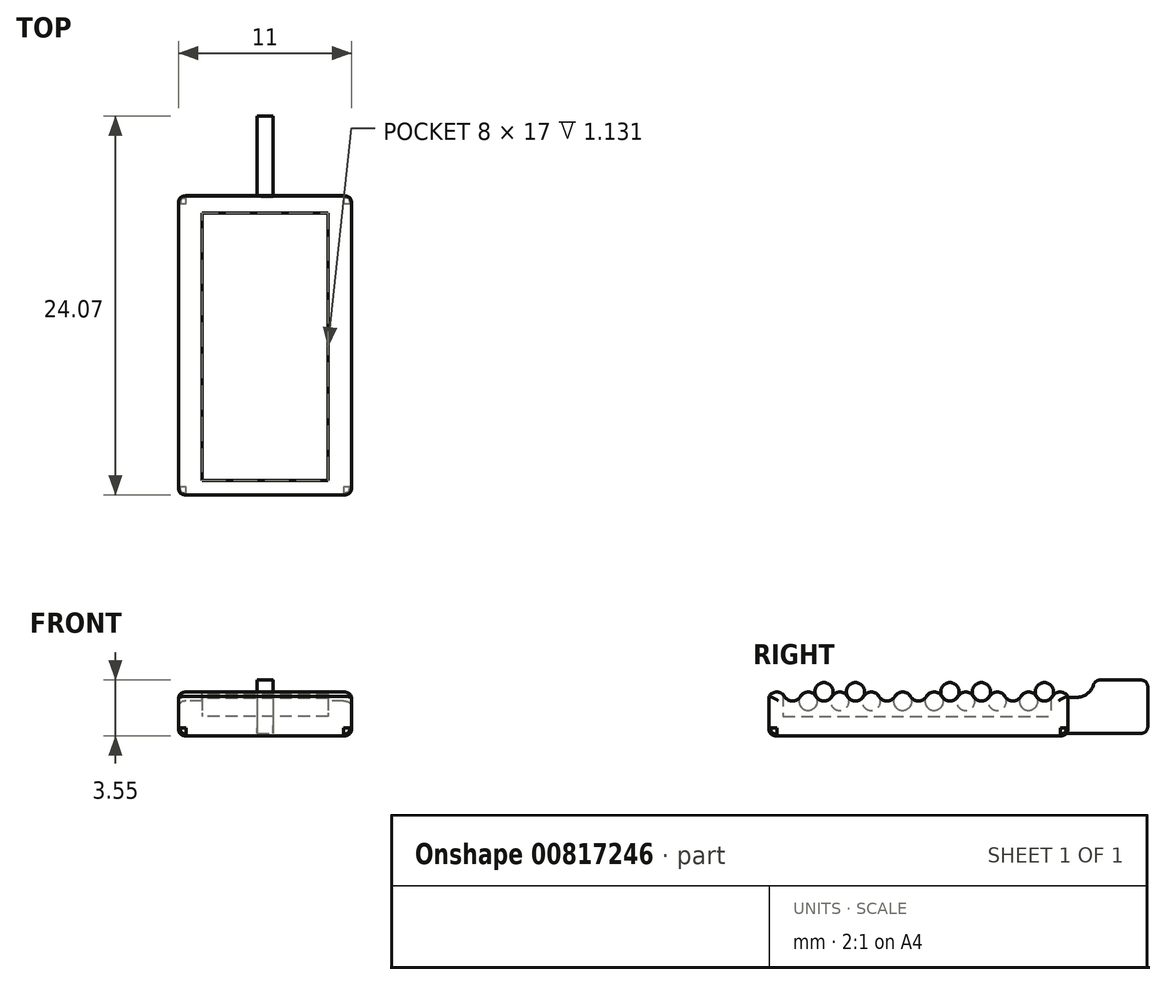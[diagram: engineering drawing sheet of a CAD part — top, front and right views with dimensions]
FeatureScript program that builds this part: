
annotation { "Feature Type Name" : "Feature", "Feature Type Description" : "" }
export const myFeature = defineFeature(function(context is Context, id is Id, definition is map)
    precondition{}
    {
        {
            var Q0;
            Q0=qCreatedBy(makeId("Right.planeOp"),FACE);
            var sketch = newSketch(context, id + "F0", { "sketchPlane" : qUnion([Q0])});
            skLineSegment(sketch, "E0.bottom", {"start": v(9.6, -1.25) * mm, "end": v(-9.4, -1.25) * mm});
            skArc(sketch, "E1.18.0.0", {"start": v(9.59, 1.26) * mm, "mid": v(9.09, 1.53) * mm, "end": v(8.6, 1.25) * mm});
            skLineSegment(sketch, "E2", {"start": v(-9.4, 1.25) * mm, "end": v(-9.4, 1.25) * mm});
            skArc(sketch, "E3.2.0.0", {"start": v(7.6, 1.25) * mm, "mid": v(7.1, 1.53) * mm, "end": v(6.6, 1.25) * mm});
            skArc(sketch, "E3.4.0.0", {"start": v(5.6, 1.25) * mm, "mid": v(5.1, 1.53) * mm, "end": v(4.6, 1.25) * mm});
            skArc(sketch, "E3.6.0.0", {"start": v(3.6, 1.25) * mm, "mid": v(3.1, 1.53) * mm, "end": v(2.6, 1.25) * mm});
            skArc(sketch, "E3.8.0.0", {"start": v(1.6, 1.25) * mm, "mid": v(1.1, 1.53) * mm, "end": v(0.6, 1.25) * mm});
            skArc(sketch, "E3.10.0.0", {"start": v(-0.4, 1.25) * mm, "mid": v(-0.9, 1.53) * mm, "end": v(-1.4, 1.25) * mm});
            skArc(sketch, "E3.12.0.0", {"start": v(-2.4, 1.25) * mm, "mid": v(-2.9, 1.53) * mm, "end": v(-3.4, 1.25) * mm});
            skArc(sketch, "E3.14.0.0", {"start": v(-4.4, 1.25) * mm, "mid": v(-4.9, 1.53) * mm, "end": v(-5.4, 1.25) * mm});
            skArc(sketch, "E3.16.0.0", {"start": v(-6.4, 1.25) * mm, "mid": v(-6.9, 1.53) * mm, "end": v(-7.4, 1.25) * mm});
            skArc(sketch, "E3.18.0.0", {"start": v(-8.4, 1.25) * mm, "mid": v(-8.9, 1.53) * mm, "end": v(-9.4, 1.26) * mm});
            skArc(sketch, "E4.MirrorCS", {"start": v(-1.4, 1.25) * mm, "mid": v(-1.9, 0.97) * mm, "end": v(-2.4, 1.25) * mm});
            skArc(sketch, "E5.MirrorCS", {"start": v(0.6, 1.25) * mm, "mid": v(0.1, 0.97) * mm, "end": v(-0.4, 1.25) * mm});
            skArc(sketch, "E6.MirrorCS", {"start": v(2.6, 1.25) * mm, "mid": v(2.1, 0.97) * mm, "end": v(1.6, 1.25) * mm});
            skArc(sketch, "E7.MirrorCS", {"start": v(4.6, 1.25) * mm, "mid": v(4.1, 0.97) * mm, "end": v(3.6, 1.25) * mm});
            skArc(sketch, "E8.MirrorCS", {"start": v(6.6, 1.25) * mm, "mid": v(6.1, 0.97) * mm, "end": v(5.6, 1.25) * mm});
            skArc(sketch, "E9.MirrorCS", {"start": v(8.6, 1.25) * mm, "mid": v(8.1, 0.97) * mm, "end": v(7.6, 1.25) * mm});
            skArc(sketch, "E10.MirrorCS", {"start": v(-3.4, 1.25) * mm, "mid": v(-3.9, 0.97) * mm, "end": v(-4.4, 1.25) * mm});
            skArc(sketch, "E11.MirrorCS", {"start": v(-5.4, 1.25) * mm, "mid": v(-5.9, 0.97) * mm, "end": v(-6.4, 1.25) * mm});
            skArc(sketch, "E12.MirrorCS", {"start": v(-7.4, 1.25) * mm, "mid": v(-7.9, 0.97) * mm, "end": v(-8.4, 1.25) * mm});
            skLineSegment(sketch, "E13", {"start": v(9.6, 1.24) * mm, "end": v(9.6, -1.25) * mm});
            skLineSegment(sketch, "E14", {"start": v(-9.4, 1.24) * mm, "end": v(-9.4, -1.25) * mm});
            skPoint(sketch, "E15.visualSharp", {"position": v(-9.4, 1.25) * mm});
            skArc(sketch, "E15.filletArc", {"start": v(-9.4, 1.26) * mm, "mid": v(-9.4, 1.25) * mm, "end": v(-9.4, 1.24) * mm});
            skPoint(sketch, "E16.visualSharp", {"position": v(9.6, 1.25) * mm});
            skArc(sketch, "E16.filletArc", {"start": v(9.6, 1.24) * mm, "mid": v(9.6, 1.25) * mm, "end": v(9.59, 1.26) * mm});
            skSolve(sketch);
        }
        {
            var Q0;
            Q0 = qSketchRegion(id + "F0", true);
            extrude(context, id + "F1", {"entities" : qUnion([Q0]), "depth" : 11 * mm, "offsetDistance" : 25 * mm});
        }
        {
            var Q0;
            Q0=qCreatedBy(makeId("Top.planeOp"),FACE);
            var sketch = newSketch(context, id + "F2", { "sketchPlane" : qUnion([Q0])});
            skLineSegment(sketch, "E17", {"start": v(0, 0) * mm, "end": v(11, 0) * mm});
            skLineSegment(sketch, "E18.bottom", {"start": v(9.5, -8.5) * mm, "end": v(1.5, -8.5) * mm});
            skLineSegment(sketch, "E18.top", {"start": v(9.5, 8.5) * mm, "end": v(1.5, 8.5) * mm});
            skLineSegment(sketch, "E18.left", {"start": v(9.5, -8.5) * mm, "end": v(9.5, 8.5) * mm});
            skLineSegment(sketch, "E18.right", {"start": v(1.5, -8.5) * mm, "end": v(1.5, 8.5) * mm});
            skPoint(sketch, "E18.middle", {"position": v(5.5, 0) * mm});
            skSolve(sketch);
        }
        {
            var Q0;
            Q0 = qSketchRegion(id + "F2", true);
            extrude(context, id + "F3", {"entities" : qUnion([Q0]), "operationType" : NewBodyOperationType.REMOVE, "endBound" : BoundingType.THROUGH_ALL, "depth" : 25 * mm, "offsetDistance" : 25 * mm});
        }
        {
            var Q0;
            Q0=qCreatedBy(makeId("Top.planeOp"),FACE);
            var sketch = newSketch(context, id + "F4", { "sketchPlane" : qUnion([Q0])});
            skLineSegment(sketch, "E19.bottom", {"start": v(5, 14.66) * mm, "end": v(6, 14.66) * mm});
            skLineSegment(sketch, "E19.top", {"start": v(5, 9.16) * mm, "end": v(6, 9.16) * mm});
            skLineSegment(sketch, "E19.left", {"start": v(5, 14.66) * mm, "end": v(5, 9.16) * mm});
            skLineSegment(sketch, "E19.right", {"start": v(6, 14.66) * mm, "end": v(6, 9.16) * mm});
            skSolve(sketch);
        }
        {
            var Q0;
            Q0 = qSketchRegion(id + "F4", true);
            extrude(context, id + "F5", {"entities" : qUnion([Q0]), "operationType" : NewBodyOperationType.ADD, "depth" : 1.2 * mm, "offsetDistance" : 25 * mm, "hasSecondDirection" : true, "secondDirectionOppositeDirection" : true, "secondDirectionDepth" : 1.1 * mm});
        }
        {
            var Q0;
            Q0=makeQuery(id+"F5.opExtrude","SWEPT_FACE",FACE,{"disambiguationData":[OSD([sQuery(id+"F4.wireOp",EDGE,"E19.left")])]});
            var sketch = newSketch(context, id + "F6", { "sketchPlane" : qUnion([Q0])});
            skLineSegment(sketch, "E20.bottom", {"start": v(-14.66, 0.05) * mm, "end": v(-10.15, 0.05) * mm});
            skLineSegment(sketch, "E20.top", {"start": v(-14.66, 2.3) * mm, "end": v(-11.25, 2.3) * mm});
            skLineSegment(sketch, "E20.left", {"start": v(-14.66, 0.05) * mm, "end": v(-14.66, 2.3) * mm});
            skLineSegment(sketch, "E20.right", {"start": v(-10.15, 0.05) * mm, "end": v(-10.15, 1.2) * mm});
            skArc(sketch, "E21", {"start": v(-11.25, 2.3) * mm, "mid": v(-10.93, 1.52) * mm, "end": v(-10.15, 1.2) * mm});
            skSolve(sketch);
        }
        {
            var Q0;
            Q0 = qSketchRegion(id + "F6", true);
            extrude(context, id + "F7", {"entities" : qUnion([Q0]), "operationType" : NewBodyOperationType.ADD, "oppositeDirection" : true, "depth" : 1 * mm, "offsetDistance" : 25 * mm});
        }
        {
            var Q0;
            Q0=makeQuery(id+"F1.opExtrude","SWEPT_FACE",FACE,{"disambiguationData":[OSD([sQuery(id+"F0.wireOp",EDGE,"E0.bottom")])]});
            var Q1;
            Q1=makeQuery(id+"F1.opExtrude","CAP_FACE",FACE,{"disambiguationData":[OSD([sQuery(id+"F0.wireOp",EDGE,"E0.bottom"),sQuery(id+"F0.wireOp",EDGE,"E1.18.0.0"),sQuery(id+"F0.wireOp",EDGE,"E3.2.0.0"),sQuery(id+"F0.wireOp",EDGE,"E3.4.0.0"),sQuery(id+"F0.wireOp",EDGE,"E3.6.0.0"),sQuery(id+"F0.wireOp",EDGE,"E3.8.0.0"),sQuery(id+"F0.wireOp",EDGE,"E3.10.0.0"),sQuery(id+"F0.wireOp",EDGE,"E3.12.0.0"),sQuery(id+"F0.wireOp",EDGE,"E3.14.0.0"),sQuery(id+"F0.wireOp",EDGE,"E3.16.0.0"),sQuery(id+"F0.wireOp",EDGE,"E3.18.0.0"),sQuery(id+"F0.wireOp",EDGE,"E4.MirrorCS"),sQuery(id+"F0.wireOp",EDGE,"E5.MirrorCS"),sQuery(id+"F0.wireOp",EDGE,"E6.MirrorCS"),sQuery(id+"F0.wireOp",EDGE,"E7.MirrorCS"),sQuery(id+"F0.wireOp",EDGE,"E8.MirrorCS"),sQuery(id+"F0.wireOp",EDGE,"E9.MirrorCS"),sQuery(id+"F0.wireOp",EDGE,"E10.MirrorCS"),sQuery(id+"F0.wireOp",EDGE,"E11.MirrorCS"),sQuery(id+"F0.wireOp",EDGE,"E12.MirrorCS"),sQuery(id+"F0.wireOp",EDGE,"E13"),sQuery(id+"F0.wireOp",EDGE,"E14"),sQuery(id+"F0.wireOp",EDGE,"E15.filletArc"),sQuery(id+"F0.wireOp",EDGE,"E16.filletArc")])],"isStart":false});
            var Q2;
            Q2=makeQuery(id+"F1.opExtrude","CAP_FACE",FACE,{"disambiguationData":[OSD([sQuery(id+"F0.wireOp",EDGE,"E0.bottom"),sQuery(id+"F0.wireOp",EDGE,"E1.18.0.0"),sQuery(id+"F0.wireOp",EDGE,"E3.2.0.0"),sQuery(id+"F0.wireOp",EDGE,"E3.4.0.0"),sQuery(id+"F0.wireOp",EDGE,"E3.6.0.0"),sQuery(id+"F0.wireOp",EDGE,"E3.8.0.0"),sQuery(id+"F0.wireOp",EDGE,"E3.10.0.0"),sQuery(id+"F0.wireOp",EDGE,"E3.12.0.0"),sQuery(id+"F0.wireOp",EDGE,"E3.14.0.0"),sQuery(id+"F0.wireOp",EDGE,"E3.16.0.0"),sQuery(id+"F0.wireOp",EDGE,"E3.18.0.0"),sQuery(id+"F0.wireOp",EDGE,"E4.MirrorCS"),sQuery(id+"F0.wireOp",EDGE,"E5.MirrorCS"),sQuery(id+"F0.wireOp",EDGE,"E6.MirrorCS"),sQuery(id+"F0.wireOp",EDGE,"E7.MirrorCS"),sQuery(id+"F0.wireOp",EDGE,"E8.MirrorCS"),sQuery(id+"F0.wireOp",EDGE,"E9.MirrorCS"),sQuery(id+"F0.wireOp",EDGE,"E10.MirrorCS"),sQuery(id+"F0.wireOp",EDGE,"E11.MirrorCS"),sQuery(id+"F0.wireOp",EDGE,"E12.MirrorCS"),sQuery(id+"F0.wireOp",EDGE,"E13"),sQuery(id+"F0.wireOp",EDGE,"E14"),sQuery(id+"F0.wireOp",EDGE,"E15.filletArc"),sQuery(id+"F0.wireOp",EDGE,"E16.filletArc")])],"isStart":true});
            var Q3;
            Q3=makeQuery(id+"F5.opExtrude","CAP_EDGE",EDGE,{"disambiguationData":[OSD([sQuery(id+"F4.wireOp",EDGE,"E19.bottom")])],"isStart":true});
            var Q4;
            Q4=makeQuery(id+"F7.opExtrude","SWEPT_EDGE",EDGE,{"disambiguationData":[OSD([sQuery(id+"F6.wireOp",EDGE,"E20.top"),sQuery(id+"F6.wireOp",EDGE,"E20.left")])]});
            var Q5;
            Q5=makeQuery(id+"F7.opExtrude","SWEPT_EDGE",EDGE,{"disambiguationData":[OSD([sQuery(id+"F6.wireOp",EDGE,"E20.top"),sQuery(id+"F6.wireOp",EDGE,"E21")])]});
            fillet(context, id + "F8", {"entities" : qUnion([Q0, Q1, Q2, Q3, Q4, Q5]), "radius" : .5 * mm, "tangentPropagation" : true, "rho" : 0.5, "crossSection" : FilletCrossSection.CONIC, "allowEdgeOverflow" : false});
        }
    });
